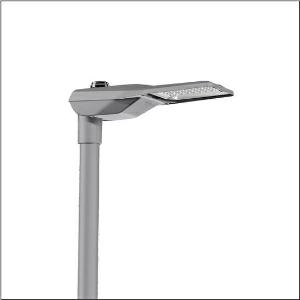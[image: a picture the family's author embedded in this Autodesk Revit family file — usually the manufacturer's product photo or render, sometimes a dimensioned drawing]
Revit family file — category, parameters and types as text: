
# Revit family: streetlight_sl_21_mini___st0_5a_5xe6b37n08hb_16a2
name_source: partatom
category: Lighting Fixtures
units: mm (PartAtom-declared; Revit-internal decimal feet)

## family parameters
Cut with Voids When Loaded = No
Host = Face
Light Source = No
Part Type = Normal
Room Calculation Point = No
Round Connector Dimension = Use Diameter
Shared = No

## types (1)
- --- (1 x LED, 9040 lm, 66 W, 3000K)
    Apparent Load = 66 VA
    CIE Flux Codes = 41 75 97 100 100
    Color Rendering = 70
    Color Temperature = 3000K
    Default Elevation = 1800 mm
    Description = Streetlight SL 21 mini, mast luminaire, primary light control with lens, of PMMA, primary optical cover: cover, of toughened safety glass, transparent, light distribution: ST0.5a, light emission: direct distribution, primary light characteristic: asymmetric, installation type: side-entry, LED, 3G 1.5mm², High Power LED, rated luminous flux: 9.040lm, luminous efficacy: 137lm/W, light colour: 730, colour temperature: 3000K, control: overheat protection, pre-setting: linear dimming characteristic, constant luminous flux control, time-dependent luminous flux control, flexible luminous flux parameterisation, mains connection: 230..240V, AC, 50/60Hz, connection cable pre-assembled, cable length: 8,5m, wiring characteristics: H07RN-F, start of lifetime: 66W, end of service life: 69W, reduction: 30W, luminaire housing, of diecast aluminium (EN AC-44300), powder-coated, Siteco® metallic grey (DB 702S), corrosivity category C5 mid according to DIN EN ISO 12944, multi-level sealing system, sealing non-destructively replaceable, inclination adjustable: 0°, 5°, 10°, 15°, length: 628mm, width: 235mm, height: 110mm, spigot size: 42mm (side-entry), protection rating (complete): IP66, insulation class (complete): insulation class I (protective earthing), certification: CE, ENEC, ENEC+, VDE, impact resistance: IK09, permissible operating ambient temperature for outdoor applications: -40..+50°C, standard-compliant lighting for roads and squares, packaging unit: 1 piece

Light Distribution: ST0.5a
    Height = 110 mm
    Lamp = 1 x LED
    Lamp Light Flux = 9040 lm
    Lamp Power = 66 W
    Lamp count = 1
    Length = 625 mm
    Luminous efficacy = 137 lm/W
    Manufacturer = Siteco
    ModVariant = No
    Model = 5XE6B37N08HB
    Number of Poles = 1
    OnlyDefault = Yes
    Power Factor = 1
    Product Name = Streetlight SL 21 mini | ST0.5a
    Product group = mast luminaire | pylon top
    ProductGroupID = 6100
    Protection Class = Protection class I
    Protection Degree = IP 66
    RLX_Detail_Level = 1
    RLX_Emergency_Light_Flux = 0 lm
    RLX_Emergency_Type = 0
    RLX_Emergency_Type_DB = No
    RlxData = <blob elided: 103149 chars, md5=afd4624b>
    Socket = socket
    Standby Power = 0 W
    System Light Flux = 9040 lm
    System Power = 66 W
    Type Comments = factory setting: luminous flux: 100 % | dim-lin: 254 | 670 mA
    Type Image = l_1294379.jpg
    URL = http://relux.com
    VarID = @adj_107299
    Voltage = 0 V
    Weight = 0.00 kg
    Width = 234 mm

## geometry (parser evidence)
native form markers: Blend x4, Sweep x8
no freeform markers — native parametric forms only
